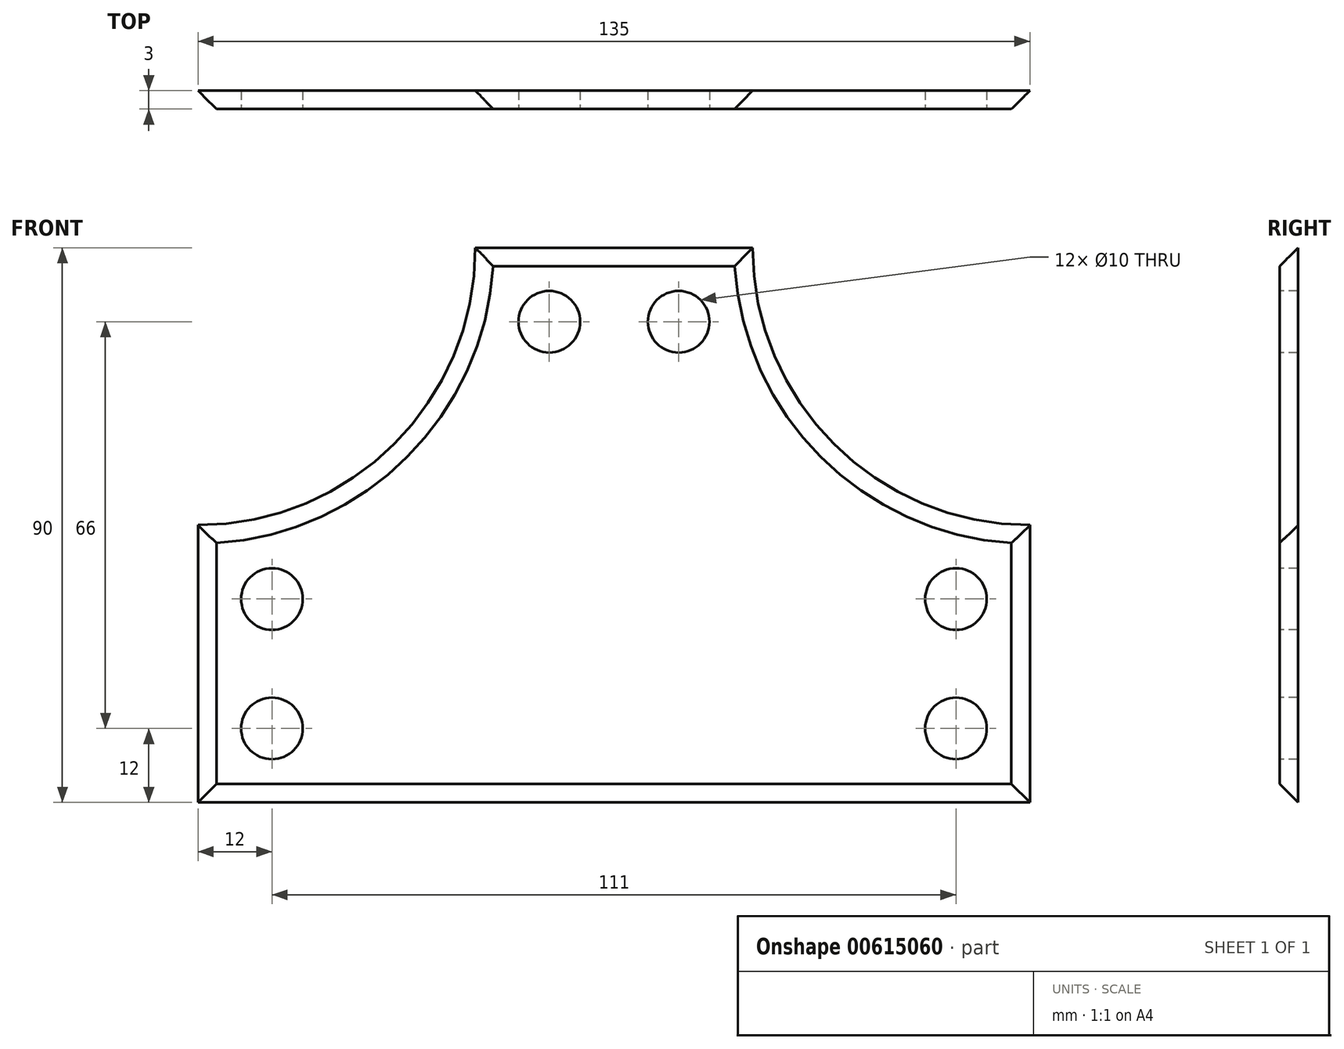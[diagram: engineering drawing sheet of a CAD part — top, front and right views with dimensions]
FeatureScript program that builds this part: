
annotation { "Feature Type Name" : "Feature", "Feature Type Description" : "" }
export const myFeature = defineFeature(function(context is Context, id is Id, definition is map)
    precondition{}
    {
        {
            var Q0;
            Q0=qCreatedBy(makeId("Front.planeOp"),FACE);
            var sketch = newSketch(context, id + "F0", { "sketchPlane" : qUnion([Q0])});
            skLineSegment(sketch, "E0", {"start": v(0, 0) * mm, "end": v(135, 0) * mm});
            skLineSegment(sketch, "E1", {"start": v(135, 0) * mm, "end": v(135, 45) * mm});
            skArc(sketch, "E2", {"start": v(90, 90) * mm, "mid": v(103.18, 58.18) * mm, "end": v(135, 45) * mm});
            skLineSegment(sketch, "E3", {"start": v(0, 0) * mm, "end": v(0, 45) * mm});
            skArc(sketch, "E4", {"start": v(0, 45) * mm, "mid": v(31.82, 58.18) * mm, "end": v(45, 90) * mm});
            skLineSegment(sketch, "E5", {"start": v(45, 90) * mm, "end": v(90, 90) * mm});
            skSolve(sketch);
        }
        {
            var Q0;
            Q0 = qSketchRegion(id + "F0", true);
            extrude(context, id + "F1", {"entities" : qUnion([Q0]), "depth" : 3 * mm, "offsetDistance" : 25 * mm});
        }
        {
            var Q0;
            Q0=makeQuery(id+"F1.opExtrude","CAP_FACE",FACE,{"disambiguationData":[OSD([sQuery(id+"F0.wireOp",EDGE,"E0"),sQuery(id+"F0.wireOp",EDGE,"E1"),sQuery(id+"F0.wireOp",EDGE,"E2"),sQuery(id+"F0.wireOp",EDGE,"E3"),sQuery(id+"F0.wireOp",EDGE,"E4"),sQuery(id+"F0.wireOp",EDGE,"E5")])],"isStart":false});
            var sketch = newSketch(context, id + "F2", { "sketchPlane" : qUnion([Q0])});
            skPoint(sketch, "E6", {"position": v(12, 12) * mm});
            skLineSegment(sketch, "E7", {"start": v(67.5, 90) * mm, "end": v(67.5, 0) * mm, "construction": true});
            skLineSegment(sketch, "E8", {"start": v(0, 22.5) * mm, "end": v(135, 22.5) * mm, "construction": true});
            skPoint(sketch, "E9.MirrorP", {"position": v(12, 33) * mm});
            skPoint(sketch, "E10.MirrorP", {"position": v(123, 33) * mm});
            skPoint(sketch, "E11.MirrorP", {"position": v(123, 12) * mm});
            skPoint(sketch, "E12", {"position": v(57, 78) * mm});
            skPoint(sketch, "E13.MirrorP", {"position": v(78, 78) * mm});
            skSolve(sketch);
        }
        {
            var Q0;
            Q0=sQuery(id+"F2.wireOp",VERTEX,"E12");
            var Q1;
            Q1=sQuery(id+"F2.wireOp",VERTEX,"E13.MirrorP");
            var Q2;
            Q2=sQuery(id+"F2.wireOp",VERTEX,"E10.MirrorP");
            var Q3;
            Q3=sQuery(id+"F2.wireOp",VERTEX,"E11.MirrorP");
            var Q4;
            Q4=sQuery(id+"F2.wireOp",VERTEX,"E6");
            var Q5;
            Q5=sQuery(id+"F2.wireOp",VERTEX,"E9.MirrorP");
            var Q6;
            Q6=makeQuery(id+"F1.opExtrude","SWEPT_BODY",BODY,{"disambiguationData":[OSD([sQuery(id+"F0.wireOp",EDGE,"E0"),sQuery(id+"F0.wireOp",EDGE,"E1"),sQuery(id+"F0.wireOp",EDGE,"E2"),sQuery(id+"F0.wireOp",EDGE,"E3"),sQuery(id+"F0.wireOp",EDGE,"E4"),sQuery(id+"F0.wireOp",EDGE,"E5")])]});
            hole(context, id + "F3", {"style" : HoleStyle.SIMPLE, "endStyle" : HoleEndStyle.BLIND, "holeDiameter" : 10 * mm, "majorDiameter" : 5 * mm, "holeDepth" : 9 * mm, "isTappedThrough" : true, "tappedDepth" : 5 * mm, "tapClearance" : 0, "locations" : qUnion([Q0, Q1, Q2, Q3, Q4, Q5]), "scope" : qUnion([Q6])});
        }
        {
            var Q0;
            Q0=makeQuery(id+"F1.opExtrude","CAP_EDGE",EDGE,{"disambiguationData":[OSD([sQuery(id+"F0.wireOp",EDGE,"E4")])],"isStart":false});
            var Q1;
            Q1=makeQuery(id+"F1.opExtrude","CAP_EDGE",EDGE,{"disambiguationData":[OSD([sQuery(id+"F0.wireOp",EDGE,"E5")])],"isStart":false});
            var Q2;
            Q2=makeQuery(id+"F1.opExtrude","CAP_EDGE",EDGE,{"disambiguationData":[OSD([sQuery(id+"F0.wireOp",EDGE,"E2")])],"isStart":false});
            var Q3;
            Q3=makeQuery(id+"F1.opExtrude","CAP_EDGE",EDGE,{"disambiguationData":[OSD([sQuery(id+"F0.wireOp",EDGE,"E1")])],"isStart":false});
            var Q4;
            Q4=makeQuery(id+"F1.opExtrude","CAP_EDGE",EDGE,{"disambiguationData":[OSD([sQuery(id+"F0.wireOp",EDGE,"E3")])],"isStart":false});
            var Q5;
            Q5=makeQuery(id+"F1.opExtrude","CAP_EDGE",EDGE,{"disambiguationData":[OSD([sQuery(id+"F0.wireOp",EDGE,"E0")])],"isStart":false});
            chamfer(context, id + "F4", {"entities" : qUnion([Q0, Q1, Q2, Q3, Q4, Q5]), "width" : 3 * mm, "tangentPropagation" : true});
        }
    });
